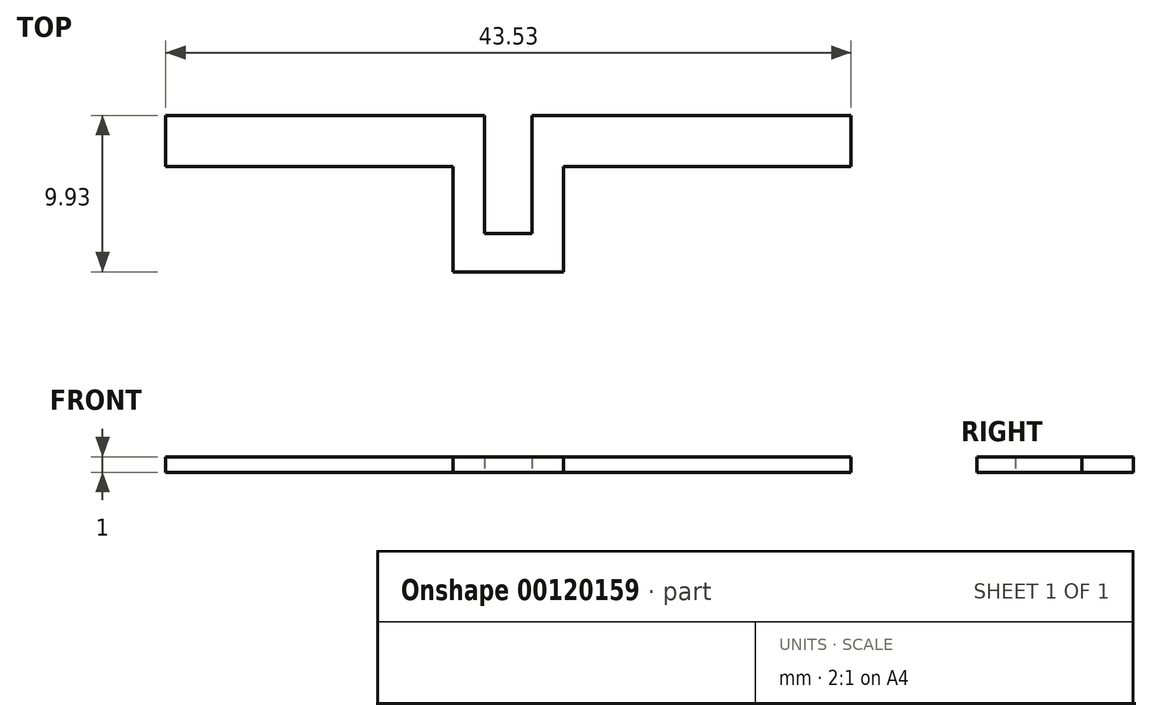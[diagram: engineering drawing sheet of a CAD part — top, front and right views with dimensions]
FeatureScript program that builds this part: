
annotation { "Feature Type Name" : "Feature", "Feature Type Description" : "" }
export const myFeature = defineFeature(function(context is Context, id is Id, definition is map)
    precondition{}
    {
        {
            var Q0;
            Q0=qCreatedBy(makeId("Top.planeOp"),FACE);
            var sketch = newSketch(context, id + "F0", { "sketchPlane" : qUnion([Q0])});
            skLineSegment(sketch, "E0", {"start": v(0, 0) * mm, "end": v(0, 7.5) * mm});
            skLineSegment(sketch, "E1", {"start": v(0, 7.5) * mm, "end": v(-20.25, 7.5) * mm});
            skLineSegment(sketch, "E2", {"start": v(-20.25, 7.5) * mm, "end": v(-20.25, 4.25) * mm});
            skLineSegment(sketch, "E3", {"start": v(-20.25, 4.25) * mm, "end": v(-2, 4.25) * mm});
            skLineSegment(sketch, "E4", {"start": v(-2, 4.25) * mm, "end": v(-2, 0) * mm});
            skLineSegment(sketch, "E5", {"start": v(-2, 0) * mm, "end": v(0, 0) * mm});
            skLineSegment(sketch, "E6", {"start": v(3.03, 0) * mm, "end": v(3.03, 7.5) * mm});
            skLineSegment(sketch, "E7", {"start": v(3.03, 7.5) * mm, "end": v(23.28, 7.5) * mm});
            skLineSegment(sketch, "E8", {"start": v(23.28, 7.5) * mm, "end": v(23.28, 4.25) * mm});
            skLineSegment(sketch, "E9", {"start": v(23.28, 4.25) * mm, "end": v(5.03, 4.25) * mm});
            skLineSegment(sketch, "E10", {"start": v(5.03, 4.25) * mm, "end": v(5.03, 0) * mm});
            skLineSegment(sketch, "E11", {"start": v(5.03, 0) * mm, "end": v(3.03, 0) * mm});
            skLineSegment(sketch, "E12.bottom", {"start": v(-2, 0) * mm, "end": v(5.03, 0) * mm});
            skLineSegment(sketch, "E12.top", {"start": v(-2, -2.43) * mm, "end": v(5.03, -2.43) * mm});
            skLineSegment(sketch, "E12.left", {"start": v(-2, 0) * mm, "end": v(-2, -2.43) * mm});
            skLineSegment(sketch, "E12.right", {"start": v(5.03, 0) * mm, "end": v(5.03, -2.43) * mm});
            skSolve(sketch);
        }
        {
            var Q0;
            Q0 = qSketchRegion(id + "F0", true);
            extrude(context, id + "F1", {"entities" : qUnion([Q0]), "depth" : 1 * mm});
        }
    });
